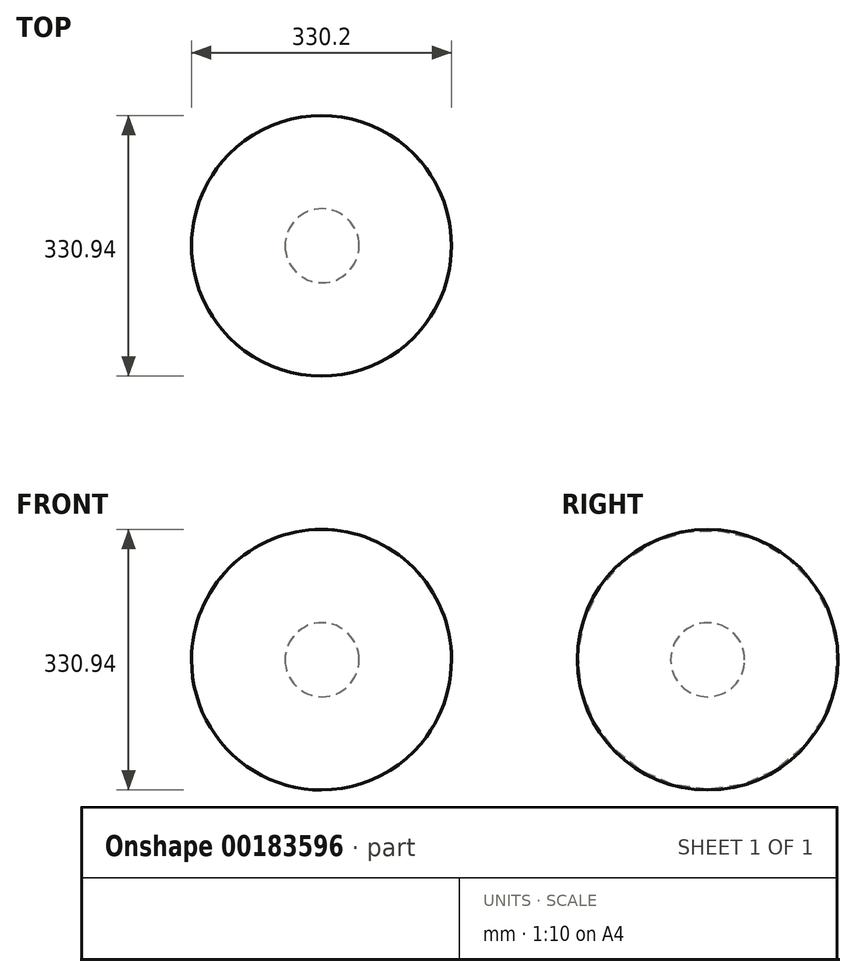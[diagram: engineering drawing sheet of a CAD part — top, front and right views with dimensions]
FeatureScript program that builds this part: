
annotation { "Feature Type Name" : "Feature", "Feature Type Description" : "" }
export const myFeature = defineFeature(function(context is Context, id is Id, definition is map)
    precondition{}
    {
        {
            var Q0;
            Q0=qCreatedBy(makeId("Front.planeOp"),FACE);
            var sketch = newSketch(context, id + "F0", { "sketchPlane" : qUnion([Q0])});
            skLineSegment(sketch, "E0", {"start": v(-165.88, 0) * mm, "end": v(164.32, 0) * mm});
            skArc(sketch, "E1", {"start": v(164.32, 0) * mm, "mid": v(-0.78, 164.73) * mm, "end": v(-165.88, 0) * mm});
            skPoint(sketch, "E2.end.orphan", {"position": v(-104.08, 0) * mm});
            skPoint(sketch, "E2.start.orphan", {"position": v(94.98, 0) * mm});
            skCircle(sketch, "E3", {"center": v(0, 0) * mm, "radius": 47 * mm});
            skSolve(sketch);
        }
        {
            var Q0;
            Q0=makeQuery(id+"F0.imprint","IMPRINT",FACE,{"disambiguationData":[TD([[makeQuery(id+"F0.imprint","IMPRINT",EDGE,{"derivedFrom":sQuery(id+"F0.wireOp",EDGE,"E0")}),1.0]])]});
            var Q1;
            Q1=sQuery(id+"F0.wireOp",EDGE,"E0");
            revolve(context, id + "F1", {"entities" : qUnion([Q0]), "axis" : qUnion([Q1]), "revolveType" : RevolveType.FULL});
        }
    });
